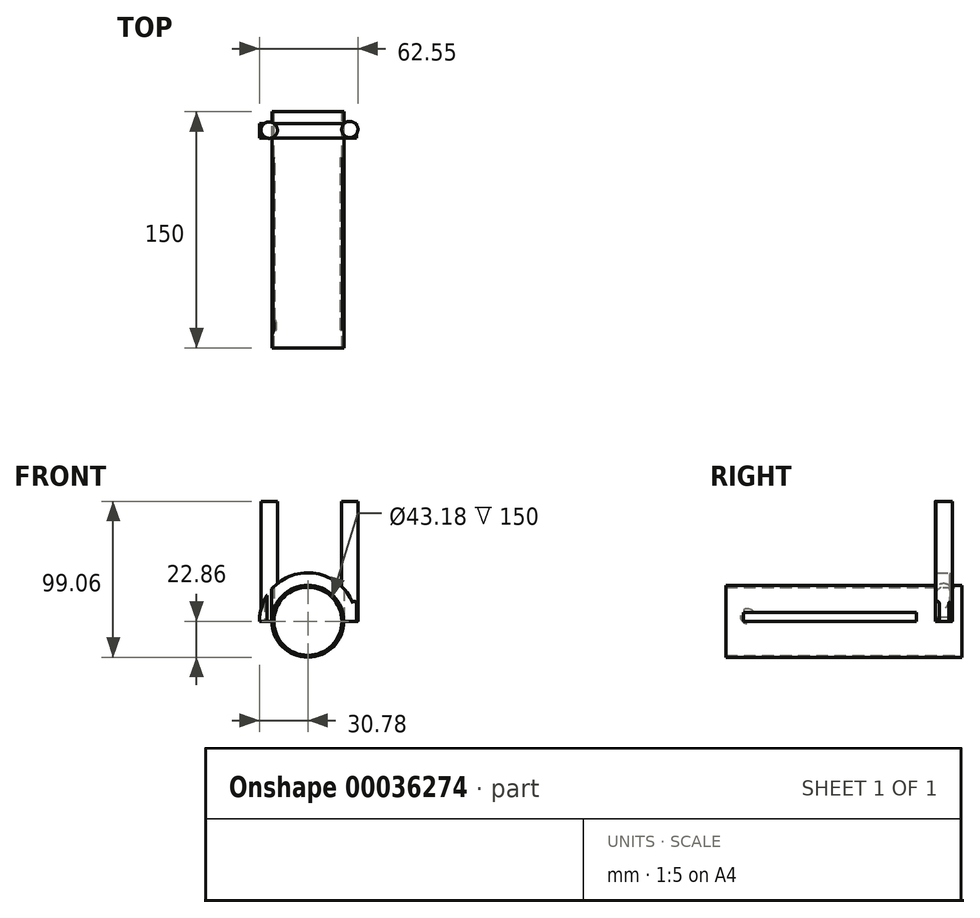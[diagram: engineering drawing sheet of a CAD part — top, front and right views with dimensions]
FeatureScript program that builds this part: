
annotation { "Feature Type Name" : "Feature", "Feature Type Description" : "" }
export const myFeature = defineFeature(function(context is Context, id is Id, definition is map)
    precondition{}
    {
        {
            var Q0;
            Q0=qCreatedBy(makeId("Front.planeOp"),FACE);
            var sketch = newSketch(context, id + "F0", { "sketchPlane" : qUnion([Q0])});
            skCircle(sketch, "E0", {"center": v(0, 0) * mm, "radius": 22.86 * mm});
            skCircle(sketch, "E1", {"center": v(0, 0) * mm, "radius": 21.59 * mm});
            skSolve(sketch);
        }
        {
            var Q0;
            Q0=makeQuery(id+"F0.imprint","IMPRINT",FACE,{"disambiguationData":[TD([[makeQuery(id+"F0.imprint","IMPRINT",EDGE,{"derivedFrom":sQuery(id+"F0.wireOp",EDGE,"E0")}),1.0]])]});
            extrude(context, id + "F1", {"entities" : qUnion([Q0]), "depth" : 150 * mm});
        }
        {
            var Q0;
            Q0=qCreatedBy(makeId("Right.planeOp"),FACE);
            var sketch = newSketch(context, id + "F2", { "sketchPlane" : qUnion([Q0])});
            skLineSegment(sketch, "E2.bottom", {"start": v(-29.04, 0) * mm, "end": v(-138.66, 0) * mm});
            skLineSegment(sketch, "E2.top", {"start": v(-29.04, 5.72) * mm, "end": v(-138.66, 5.72) * mm});
            skLineSegment(sketch, "E2.left", {"start": v(-29.04, 0) * mm, "end": v(-29.04, 5.72) * mm});
            skLineSegment(sketch, "E2.right", {"start": v(-138.66, 0) * mm, "end": v(-138.66, 5.72) * mm});
            skSolve(sketch);
        }
        {
            var Q0;
            Q0 = qSketchRegion(id + "F2", true);
            extrude(context, id + "F3", {"entities" : qUnion([Q0]), "operationType" : NewBodyOperationType.REMOVE, "endBound" : BoundingType.SYMMETRIC, "oppositeDirection" : true, "depth" : 76.2 * mm});
        }
        {
            var Q0;
            Q0=qCreatedBy(makeId("Top.planeOp"),FACE);
            var sketch = newSketch(context, id + "F4", { "sketchPlane" : qUnion([Q0])});
            skLineSegment(sketch, "E3.bottom", {"start": v(14.56, -7.58) * mm, "end": v(30.78, -7.58) * mm});
            skLineSegment(sketch, "E3.top", {"start": v(14.56, -16.73) * mm, "end": v(30.78, -16.73) * mm});
            skLineSegment(sketch, "E3.left", {"start": v(14.56, -7.58) * mm, "end": v(14.56, -16.73) * mm});
            skLineSegment(sketch, "E3.right", {"start": v(30.78, -7.58) * mm, "end": v(30.78, -16.73) * mm});
            skSolve(sketch);
        }
        {
            var Q0;
            Q0 = qSketchRegion(id + "F4", true);
            extrude(context, id + "F5", {"entities" : qUnion([Q0]), "operationType" : NewBodyOperationType.ADD, "depth" : 12.7 * mm});
        }
        {
            var Q0;
            {var subQ0=sQuery(id+"F4.wireOp",EDGE,"E3.right");var subQ1=sQuery(id+"F0B8wNnZoACMYPZ_1.wireOp",EDGE,"0657b783-154f-4117-873f-c8229050e505");Q0=makeQuery(id+"FjSrg42h6ONFkE3_1.boolean.opBoolean","SPLIT",EDGE,{"disambiguationData":[TD([makeQuery(id+"F5.opExtrude","CAP_FACE",FACE,{"disambiguationData":[OSD([sQuery(id+"F4.wireOp",EDGE,"E3.bottom"),sQuery(id+"F4.wireOp",EDGE,"E3.top"),sQuery(id+"F4.wireOp",EDGE,"E3.left"),subQ0])],"isStart":true}),makeQuery(id+"F5.opExtrude","SWEPT_FACE",FACE,{"disambiguationData":[OSD([subQ0])]}),makeQuery(id+"FjSrg42h6ONFkE3_1.opExtrude","SWEPT_FACE",FACE,{"disambiguationData":[OSD([subQ1])]}),makeQuery(id+"FjSrg42h6ONFkE3_1.opExtrude","CAP_FACE",FACE,{"disambiguationData":[OSD([subQ1])],"isStart":true})])],"derivedFrom":makeQuery(id+"F5.opExtrude","CAP_EDGE",EDGE,{"disambiguationData":[OSD([subQ0])],"isStart":true})});}
            var Q1;
            Q1=makeQuery(id+"F5.opExtrude","CAP_EDGE",EDGE,{"disambiguationData":[OSD([sQuery(id+"F4.wireOp",EDGE,"E3.left")])],"isStart":false});
            var Q2;
            Q2=makeQuery(id+"F5.opExtrude","CAP_EDGE",EDGE,{"disambiguationData":[OSD([sQuery(id+"F4.wireOp",EDGE,"E3.top")])],"isStart":false});
            var Q3;
            Q3=makeQuery(id+"F5.opExtrude","CAP_EDGE",EDGE,{"disambiguationData":[OSD([sQuery(id+"F4.wireOp",EDGE,"E3.bottom")])],"isStart":false});
            var Q4;
            Q4=makeQuery(id+"F5.opExtrude","CAP_EDGE",EDGE,{"disambiguationData":[OSD([sQuery(id+"F4.wireOp",EDGE,"E3.right")])],"isStart":false});
            fillet(context, id + "F6", {"entities" : qUnion([Q0, Q1, Q2, Q3, Q4]), "radius" : 1.27 * mm, "tangentPropagation" : true, "allowEdgeOverflow" : false});
        }
        {
            var Q0;
            Q0 = qSketchRegion(id + "F4", true);
            var Q1;
            Q1=makeQuery(id+"F1.opExtrude","CAP_EDGE",EDGE,{"disambiguationData":[OSD([sQuery(id+"F0.wireOp",EDGE,"E0")])],"isStart":true});
            revolve(context, id + "F7", {"operationType" : NewBodyOperationType.ADD, "entities" : qUnion([Q0]), "axis" : qUnion([Q1]), "revolveType" : RevolveType.ONE_DIRECTION, "angle" : 180 * degree});
        }
        {
            var Q0;
            Q0=qCreatedBy(makeId("Top.planeOp"),FACE);
            var sketch = newSketch(context, id + "F8", { "sketchPlane" : qUnion([Q0])});
            skCircle(sketch, "E4", {"center": v(-24.54, -11.74) * mm, "radius": 5.21 * mm});
            skCircle(sketch, "E5", {"center": v(26.62, -11.32) * mm, "radius": 5.15 * mm});
            skSolve(sketch);
        }
        {
            var Q0;
            Q0 = qSketchRegion(id + "F8", true);
            extrude(context, id + "F9", {"entities" : qUnion([Q0]), "operationType" : NewBodyOperationType.ADD, "depth" : 76.2 * mm});
        }
        {
            var Q0;
            Q0=qCreatedBy(makeId("Right.planeOp"),FACE);
            var sketch = newSketch(context, id + "F10", { "sketchPlane" : qUnion([Q0])});
            skCircle(sketch, "E6", {"center": v(-136.1, 3.22) * mm, "radius": 4.7 * mm});
            skSolve(sketch);
        }
        {
            var Q0;
            Q0 = qSketchRegion(id + "F10", true);
            extrude(context, id + "F11", {"entities" : qUnion([Q0]), "operationType" : NewBodyOperationType.REMOVE, "oppositeDirection" : true, "depth" : 25.4 * mm});
        }
        {
            var Q0;
            {var subQ0=sQuery(id+"F4.wireOp",EDGE,"E3.bottom");Q0=makeQuery(id+"F7.boolean.opBoolean","MERGE",FACE,{"derivedFrom":[makeQuery(id+"F5.boolean.opBoolean","SPLIT",FACE,{"disambiguationData":[TD([makeQuery(id+"F1.opExtrude","SWEPT_FACE",FACE,{"disambiguationData":[OSD([sQuery(id+"F0.wireOp",EDGE,"E1")])]})])],"derivedFrom":makeQuery(id+"F5.opExtrude","SWEPT_FACE",FACE,{"disambiguationData":[OSD([subQ0])]})}),makeQuery(id+"F7.opRevolve","SWEPT_FACE",FACE,{"disambiguationData":[OSD([subQ0])]})]});}
            extrude(context, id + "F12", {"entities" : qUnion([Q0]), "operationType" : NewBodyOperationType.REMOVE, "endBound" : BoundingType.SYMMETRIC, "oppositeDirection" : true, "depth" : 25.4 * mm});
        }
    });
